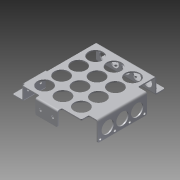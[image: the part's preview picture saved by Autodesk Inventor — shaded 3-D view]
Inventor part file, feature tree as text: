
AUTODESK INVENTOR PART (.ipt)
format: ipt  version: 2013 (Build 170138000, 138)  size: 630,784 bytes
history: native  units: in
note: dims shown in document units (in); Inventor stores cm internally (conversion verified against a paired STEP export)
features: sheet_metal_op x21, other x15, sketch x13, chamfer x2, reference x2
ambient origin geometry x8: Origin, YZ Plane, XZ Plane, XY Plane, X Axis, Y Axis, Z Axis, Center Point
bodies: Solid1 (feature_tree)
feature tree (53):
  sheet_metal_op  "Face1"
  sheet_metal_op  "Flange1"
  sheet_metal_op  "Flange2"
  sketch  "Sketch4"  dims[d3=0.5in]
  sheet_metal_op  "Face2"
  sheet_metal_op  "Flange3"
  sheet_metal_op  "Flange4"
  chamfer  "Corner Round1"
  sheet_metal_op  "Flange5"
  sheet_metal_op  "Flange6"
  chamfer  "Corner Round2"
  sketch  "Sketch1"  dims[d0=1.0in]
  other  "Plate1"
  sketch  "Sketch2"  dims[d1=6.0in]
  other  "Plate2"
  sheet_metal_op  "Bend1"
  sheet_metal_op  "Corner1"
  sketch  "Sketch3"  dims[d2=0.26in]
  other  "Plate3"
  sheet_metal_op  "Bend2"
  sheet_metal_op  "Corner2"
  other  "Plate4"
  sheet_metal_op  "Bend3"
  sketch  "Sketch5"  dims[d4=2.3622in d6=1.0in d7=0.3937in d9=1.0in]
  other  "Plate5"
  sheet_metal_op  "Bend4"
  sheet_metal_op  "Corner3"
  sketch  "Sketch6"  dims[d11=0.5in]
  other  "Plate6"
  sheet_metal_op  "Bend5"
  sheet_metal_op  "Corner4"
  sketch  "Sketch7"  dims[d12=0.125in]
  sketch  "Sketch8"  dims[d13=0.125in]
  sketch  "Sketch9"  dims[d14=0.0625in]
  other  "Plate7"
  sheet_metal_op  "Bend6"
  sheet_metal_op  "Corner5"
  sketch  "Sketch10"  dims[d15=0.25in]
  other  "Plate8"
  sheet_metal_op  "Bend7"
  sheet_metal_op  "Corner6"
  reference  "Reference10"
  reference  "Reference11"
  sketch  "Sketch11"  dims[d16=0.125in]
  sketch  "Sketch12"  dims[d17=1.5in d18=90.0deg d19=0.05in]
  sketch  "Sketch13"  dims[d20=0.5in d21=0.125in d22=0.125in d23=0.125in d24=0.0625in d25=0.25in d26=0.125in d27=7.625in d28=90.0deg d29=0.05in d30=0.5in d31=0.125in d32=0.125in d33=2.25in d35=0.25in d36=0.125in d37=0.125in d38=0.0625in d39=0.25in d40=0.125in d41=0.125in d42=0.0625in d43=0.25in d44=0.125in d45=1.625in d46=90.0deg d47=0.05in d48=0.5in d49=0.125in d50=0.125in d51=0.125in d52=0.0625in d53=0.25in d54=0.125in d55=1.125in d56=90.0deg d57=0.05in d58=0.5in d59=0.125in d60=0.125in d61=0.125in d62=0.0in d63=0.125in d64=1.5in d65=1.125in d66=1.125in d67=1.5748in d69=1.7333in d70=1.1811in d72=1.875in d75=1.125in d76=1.125in d77=0.125in d78=0.0in d79=0.875in d83=0.75in d84=6.0in d85=1.9685in d87=1.125in d88=0.3937in d90=1.0in d92=0.125in d93=0.0in d95=5.0in d96=0.125in d97=0.0625in d98=0.25in d99=0.125in d100=2.0in d101=90.0deg d102=0.05in d103=0.5in d104=0.125in d105=0.125in d106=0.25in d107=2.25in d108=2.0in d109=0.125in d110=0.0625in d111=0.25in d112=0.125in d113=1.5in d114=90.0deg d115=0.05in d116=0.5in d117=0.125in d118=0.125in d119=0.75in d120=0.75in d121=0.25in d122=5.0in d123=1.25in d124=1.0in d125=1.1811in d127=1.5in d128=0.3937in d130=1.0in d132=1.0in d133=0.25in d134=0.26in d135=0.25in d136=1.5748in d138=1.5in d139=0.3937in d141=1.0in d143=0.25in d144=0.125in d145=0.0in d146=7.45in d147=0.26in d149=0.5in d150=0.5in d151=0.125in d152=0.0in d153=0.26in d155=0.5in d156=0.5in d157=0.125in d158=0.0in d159=0.125in d5=0.0312in d8=0.0625in d10=0.0312in]
  other  "Cut1"
  other  "Cut2"
  other  "Cut3"
  other  "Cut4"
  other  "Cut5"
  other  "Cut6"
  other  "Definition1"
